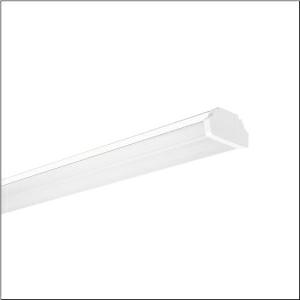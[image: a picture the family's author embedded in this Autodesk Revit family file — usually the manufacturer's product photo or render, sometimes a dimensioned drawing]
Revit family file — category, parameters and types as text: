
# Revit family: dus_r__31_ho_53bd812d2v6120_f11a
name_source: partatom
category: Lighting Fixtures
units: mm (PartAtom-declared; Revit-internal decimal feet)

## family parameters
Cut with Voids When Loaded = No
Host = Face
Light Source = No
Part Type = Normal
Room Calculation Point = No
Round Connector Dimension = Use Diameter
Shared = No

## types (1)
- --- (1 x LED, 12400 lm, 79.5 W, 6500K)
    Apparent Load = 80 VA
    CIE Flux Codes = 47 80 95 92 100
    Color Rendering = 80
    Color Temperature = 6500K
    Default Elevation = 1800 mm
    Description = DUS® 31 HO, luminaire insert, of sheet steel, coil coated, white, length: 1.535mm, width: 81mm, height: 90mm, 5x system unit, system units: 307mm, LED rated luminous flux: 12.400lm, light colour: 865, control gear: DALI 2, control gear: ECG DALI, with plug, 5-pole, with phase selection, mains connection: 220..240V, AC, 50/60Hz, rated input power: 80W, through-wiring accessed according to module size, primary optical cover: cover, of PMMA, light emission: direct distribution, primary light characteristic: symmetric, protection rating (complete): IP20, protection rating (LED compartment): IP50, insulation class (complete): insulation class I (protective earthing), certification: CE, ENEC, VDE, UKCA, impact resistance: IK03, permissible ambient temperature for indoor applications: -25..+30°C, corresponds to IFS (International Featured Standards) requirements for safety and quality in the food industry, reducing of maximum allowable ambient temperature of 5°C with ceiling mounting, packaging unit: 1 piece
    Height = 95 mm
    Lamp = 1 x LED
    Lamp Light Flux = 12400 lm
    Lamp Power = 79.5 W
    Lamp count = 1
    Length = 1535 mm
    Luminous efficacy = 156 lm/W
    Manufacturer = Siteco
    ModVariant = No
    Model = 53BD812D2V6120
    Mounting Place = Ceiling
    Mounting Type = Pendant
    Number of Poles = 1
    OnlyDefault = Yes
    Power Factor = 1
    Product Name = DUS® 31 HO
    Product group = luminaire insert
    ProductGroupID = 901
    Protection Class = Protection class I
    Protection Degree = IP 20
    RLX_Detail_Level = 1
    RLX_Emergency_Light_Flux = 0 lm
    RLX_Emergency_Type = 0
    RLX_Emergency_Type_DB = No
    RlxData = <blob elided: 41969 chars, md5=844a93da>
    Socket = socket
    Standby Power = 0 W
    System Light Flux = 12400 lm
    System Power = 80 W
    Type Comments = factory setting: luminous flux: 100 % | dim-lin: 254 | 345 mA
    Type Image = l_1003451.jpg
    URL = http://relux.com
    VarID = @adj_140103
    Voltage = 0 V
    Weight = 0.00 kg
    Width = 81 mm

## geometry (parser evidence)
native form markers: Blend x4, Sweep x11
no freeform markers — native parametric forms only
